# Revit family: LEGRAND_TOMAS SIN ENCLAVAMIENTO_DE SUPERFICIE_IP44_400
name_source: partatom
category: Installations électriques
revit_build: Autodesk Revit 2018 (Build: 20170223_1515(x64)
units: mm (PartAtom-declared; Revit-internal decimal feet)

## family parameters
Conserver l'orientation des annotations = Non
Cote de connecteur circulaire = Utiliser le diamètre
Couper avec des vides une fois chargée = Non
Hôte = Face
Partagée = Non
Point de calcul de pièce = Non
Type d'élément = Normal

## types (20) — shared parameters
Condiciones Generales de Uso = https://export.legrand.com
Description = Toma AL estándar internacional para montaje empotrado o en superficie con accesorio permite la alimentación de aparatos de potencia
Dia bouchon = 50 mm  [stored 0.164042 ft]
Elévation par défaut = 1000 mm  [stored 3.28084 ft]
Estándar CEI o NFC = CEI
Fabricant = Legrand
RAY BOUCHON = 25 mm  [stored 0.082021 ft]
Ray = 25 mm  [stored 0.082021 ft]
Temperatura maxima de instalación = 40°C
Temperatura maxima de uso = 100°C
Temperatura minima de instalación = -20°C
Temperatura minima de uso = -50°C
Tension V = 400 V  50/60 Hz rojo
clase de protección IP = IP44
color característico = rojo
instalación de empotrar E o de superficie S = empotrar y superficie
sin halogeno = Oui
tipo de conexión = conexión por tonillo

## per-type parameters (varying)
| type | Modèle | altura mm | ancho mm | distancia de fijación horizontal mm | distancia de fijación vertical mm | h1 | intensidad A | materia de la caja | numero de polos | posición de la tierra h | profundidad de empotrar mm | profundidad mm | resistencia a los choques IK |
| base para cuadro Hypra   IP44   16 A   380/415 V   2P+T   plast caja de superficie para cableado de paso | 052222 | 182 mm | 86 mm | 52 mm | 60 mm | 109 mm | 16 A | plástico | 3 | 9 | 75 mm | 115 mm | 09 |
| base para cuadro Hypra   IP44   16 A   380/415 V   3P+T   plast caja de superficie para cableado de paso | 052223 | 212 mm | 100 mm  [stored 0.328084 ft] | 60 mm | 70 mm | 127 mm | 16 A | plástico | 3 | 9 | 77 mm | 117 mm | 09 |
| base para cuadro Hypra   IP44   16 A   380/415 V   3P+N+T   plast caja de superficie para cableado de paso | 052224 | 212 mm | 100 mm  [stored 0.328084 ft] | 60 mm | 70 mm | 127 mm | 16 A | plástico | 5 | 6 | 77 mm | 121 mm | 09 |
| base para cuadro Hypra   IP44   16 A   380/415 V   2P+T   métal montaje de superficie con caja simple | 052232 | 106 mm | 74 mm | 52 mm | 60 mm | 64 mm | 16 A | metal | 3 | 9 | 58 mm | 98 mm | 10 |
| base para cuadro Hypra   IP44   16 A   380/415 V   3P+T   métal montaje de superficie con caja simple | 052233 | 122 mm  [stored 0.400262 ft] | 96 mm  [stored 0.314961 ft] | 60 mm | 70 mm | 73 mm | 16 A | metal | 4 | 6 | 60 mm | 100 mm  [stored 0.328084 ft] | 10 |
| base para cuadro Hypra   IP44   16 A   380/415 V   3P+N+T   métal montaje de superficie con caja simple | 052234 | 122 mm  [stored 0.400262 ft] | 96 mm  [stored 0.314961 ft] | 60 mm | 70 mm | 73 mm | 16 A | metal | 5 | 6 | 60 mm | 104 mm | 10 |
| base para cuadro  Hypra   IP44   32 A   380/415 V   2P+T   plast caja de superficie para cableado de paso | 052918 | 162 mm | 102 mm | 70 mm | 70 mm | 97 mm | 32 A | plástico | 3 | 9 | 90 mm  [stored 0.295276 ft] | 143 mm | 09 |
| base para cuadro Hypra   IP44   32 A   380/415 V   3P+T   plast montaje de superficie con caja simple | 052919 | 162 mm | 102 mm | 70 mm | 70 mm | 97 mm | 32 A | plástico | 4 | 6 | 90 mm  [stored 0.295276 ft] | 143 mm | 09 |
| base para cuadro Hypra   IP44   32 A   380/415 V   3P+N+T   plast montaje de superficie con caja simple | 052920 | 162 mm | 102 mm | 70 mm | 70 mm | 97 mm | 32 A | plástico | 5 | 6 | 90 mm  [stored 0.295276 ft] | 146 mm  [stored 0.479003 ft] | 09 |
| base para cuadro Hypra   IP44   32 A   380/415 V   2P+T   métal montaje de superficie con caja simple | 052932 | 162 mm | 102 mm | 70 mm | 70 mm | 97 mm | 32 A | metal | 3 | 9 | 90 mm  [stored 0.295276 ft] | 143 mm | 10 |
| base para cuadro Hypra   IP44   32 A   380/415 V   3P+T   métal montaje de superficie con caja simple | 052933 | 162 mm | 102 mm | 70 mm | 70 mm | 97 mm | 32 A | metal | 4 | 6 | 90 mm  [stored 0.295276 ft] | 143 mm | 10 |
| base para cuadro Hypra   IP44   32 A   380/415 V   3P+N+T   métal montaje de superficie con caja simple | 052934 | 162 mm | 102 mm | 70 mm | 80 mm | 97 mm | 32 A | metal | 5 | 6 | 90 mm  [stored 0.295276 ft] | 146 mm  [stored 0.479003 ft] | 10 |
| base para cuadro Hypra   IP44   63 A   380/415 V   3P+T   plast caja de superficie para cableado de paso | 053823 | 300 mm | 170 mm | 77 mm | 85 mm | 180 mm  [stored 0.590551 ft] | 63 A | plástico | 4 | 6 | 150 mm | 220 mm | 09 |
| base para cuadro Hypra   IP44   63 A   380/415 V   3P+N+T   plast caja de superficie para cableado de paso | 053824 | 300 mm | 170 mm | 77 mm | 85 mm | 180 mm  [stored 0.590551 ft] | 63 A | plástico | 4 | 6 | 150 mm | 220 mm | 09 |
| base para cuadro Hypra   IP44   16 A   380/415 V   2P+T   plast montaje de superficie con caja simple | 052222 | 106 mm | 74 mm | 52 mm | 60 mm | 64 mm | 16 A | plástico | 3 | 9 | 58 mm | 98 mm | 09 |
| base para cuadro Hypra   IP44   16 A   380/415 V   3P+T   plast montaje de superficie con caja simple | 052223 | 122 mm  [stored 0.400262 ft] | 96 mm  [stored 0.314961 ft] | 60 mm | 70 mm | 73 mm | 16 A | plástico | 3 | 9 | 60 mm | 100 mm  [stored 0.328084 ft] | 09 |
| base para cuadro Hypra   IP44   16 A   380/415 V   3P+N+T   plast montaje de superficie con caja simple | 052224 | 122 mm  [stored 0.400262 ft] | 96 mm  [stored 0.314961 ft] | 60 mm | 70 mm | 73 mm | 16 A | plástico | 5 | 6 | 60 mm | 104 mm | 09 |
| base para cuadro  Hypra   IP44   32 A   380/415 V   2P+T   plast montaje de superficie con caja simple | 052918 | 162 mm | 102 mm | 70 mm | 70 mm | 97 mm | 32 A | plástico | 3 | 9 | 90 mm  [stored 0.295276 ft] | 143 mm | 09 |
| base para cuadro Hypra   IP44   32 A   380/415 V   3P+T   plast caja de superficie para cableado de paso | 052919 | 162 mm | 102 mm | 70 mm | 70 mm | 97 mm | 32 A | plástico | 4 | 6 | 90 mm  [stored 0.295276 ft] | 143 mm | 09 |
| base para cuadro Hypra   IP44   32 A   380/415 V   3P+N+T   plast caja de superficie para cableado de paso | 052920 | 162 mm | 102 mm | 70 mm | 70 mm | 97 mm | 32 A | plástico | 5 | 6 | 90 mm  [stored 0.295276 ft] | 146 mm  [stored 0.479003 ft] | 09 |

note: [stored X ft] marks values corroborated as IEEE doubles in the binary element streams (Revit-internal decimal feet)
